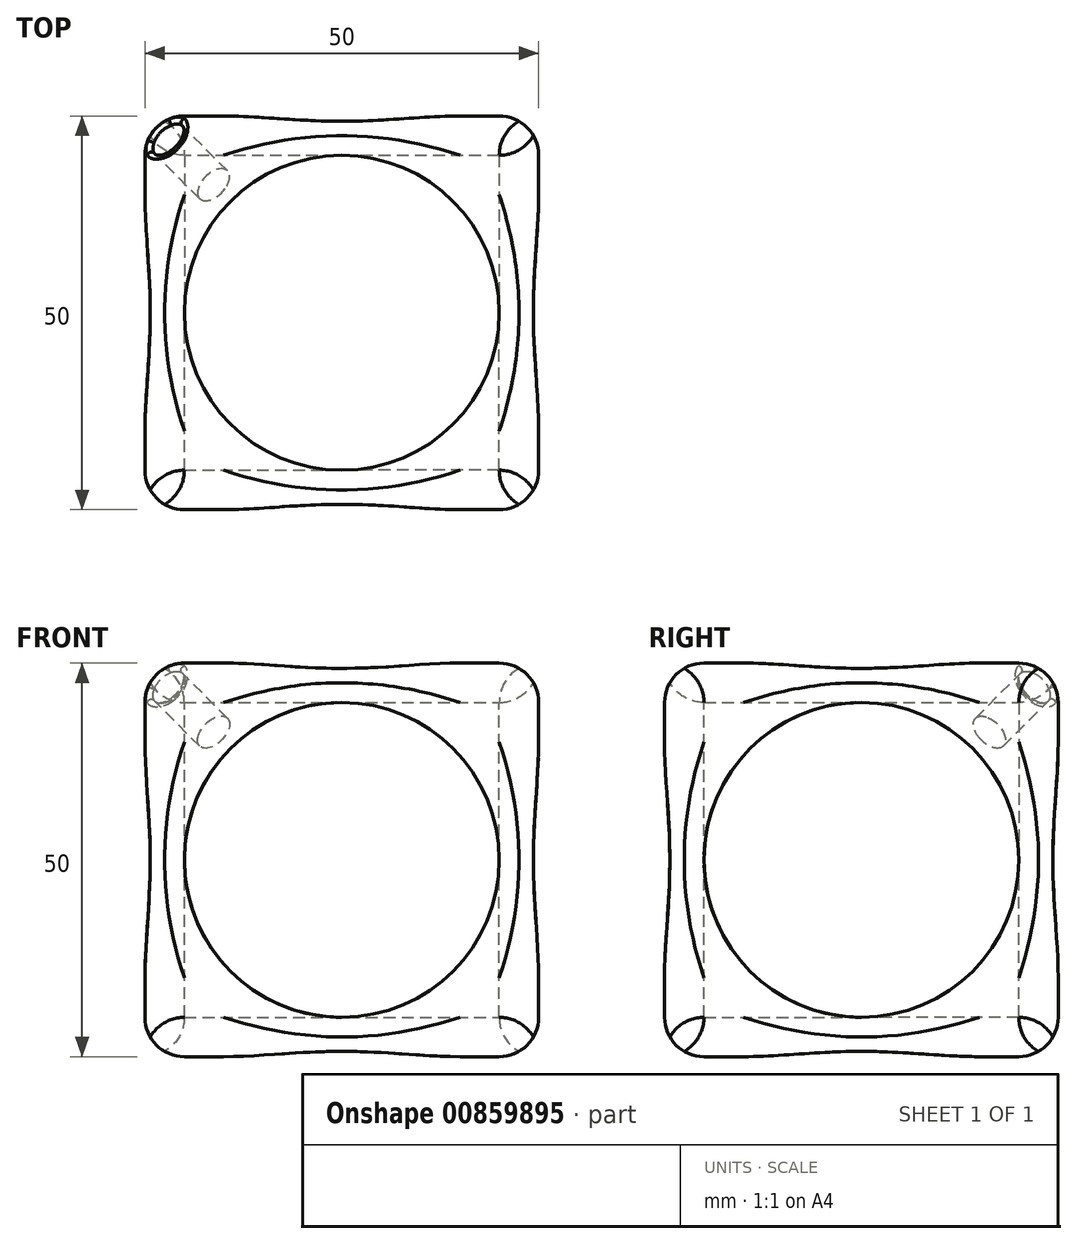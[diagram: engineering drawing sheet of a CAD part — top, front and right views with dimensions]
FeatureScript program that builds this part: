
annotation { "Feature Type Name" : "Feature", "Feature Type Description" : "" }
export const myFeature = defineFeature(function(context is Context, id is Id, definition is map)
    precondition{}
    {
        {
            var Q0;
            Q0=qCreatedBy(makeId("Top.planeOp"),FACE);
            var sketch = newSketch(context, id + "F0", { "sketchPlane" : qUnion([Q0])});
            skLineSegment(sketch, "E0.bottom", {"start": v(-25, -25) * mm, "end": v(25, -25) * mm});
            skLineSegment(sketch, "E0.top", {"start": v(-25, 25) * mm, "end": v(25, 25) * mm});
            skLineSegment(sketch, "E0.left", {"start": v(-25, -25) * mm, "end": v(-25, 25) * mm});
            skLineSegment(sketch, "E0.right", {"start": v(25, -25) * mm, "end": v(25, 25) * mm});
            skPoint(sketch, "E0.middle", {"position": v(0, 0) * mm});
            skSolve(sketch);
        }
        {
            var Q0;
            Q0 = qSketchRegion(id + "F0", true);
            extrude(context, id + "F1", {"entities" : qUnion([Q0]), "depth" : 50 * mm, "offsetDistance" : 25 * mm});
        }
        {
            var Q0;
            Q0=makeQuery(id+"F1.opExtrude","SWEPT_FACE",FACE,{"disambiguationData":[OSD([sQuery(id+"F0.wireOp",EDGE,"E0.left")])]});
            var sketch = newSketch(context, id + "F2", { "sketchPlane" : qUnion([Q0])});
            skCircle(sketch, "E1", {"center": v(0, 25) * mm, "radius": 20 * mm});
            skPoint(sketch, "E1.centerSnap0", {"position": v(25, 25) * mm});
            skSolve(sketch);
        }
        {
            var Q0;
            Q0=makeQuery(id+"F1.opExtrude","SWEPT_FACE",FACE,{"disambiguationData":[OSD([sQuery(id+"F0.wireOp",EDGE,"E0.top")])]});
            var sketch = newSketch(context, id + "F3", { "sketchPlane" : qUnion([Q0])});
            skCircle(sketch, "E2", {"center": v(0, 25) * mm, "radius": 20 * mm});
            skPoint(sketch, "E2.centerSnap0", {"position": v(25, 25) * mm});
            skSolve(sketch);
        }
        {
            var Q0;
            Q0=makeQuery(id+"F1.opExtrude","CAP_FACE",FACE,{"disambiguationData":[OSD([sQuery(id+"F0.wireOp",EDGE,"E0.bottom"),sQuery(id+"F0.wireOp",EDGE,"E0.top"),sQuery(id+"F0.wireOp",EDGE,"E0.left"),sQuery(id+"F0.wireOp",EDGE,"E0.right")])],"isStart":false});
            var sketch = newSketch(context, id + "F4", { "sketchPlane" : qUnion([Q0])});
            skCircle(sketch, "E3", {"center": v(0, 0) * mm, "radius": 20 * mm});
            skSolve(sketch);
        }
        {
            var Q0;
            Q0=makeQuery(id+"F4.imprint","IMPRINT",FACE,{"disambiguationData":[TD([[makeQuery(id+"F4.imprint","IMPRINT",EDGE,{"derivedFrom":sQuery(id+"F4.wireOp",EDGE,"E3")}),1.0]])]});
            extrude(context, id + "F5", {"entities" : qUnion([Q0]), "operationType" : NewBodyOperationType.REMOVE, "oppositeDirection" : true, "depth" : 50 * mm, "offsetDistance" : 25 * mm});
        }
        {
            var Q0;
            Q0=makeQuery(id+"F3.imprint","IMPRINT",FACE,{"disambiguationData":[TD([[makeQuery(id+"F3.imprint","IMPRINT",EDGE,{"derivedFrom":sQuery(id+"F3.wireOp",EDGE,"E2")}),1.0]])]});
            extrude(context, id + "F6", {"entities" : qUnion([Q0]), "operationType" : NewBodyOperationType.REMOVE, "oppositeDirection" : true, "depth" : 50 * mm, "offsetDistance" : 25 * mm});
        }
        {
            var Q0;
            Q0=makeQuery(id+"F2.imprint","IMPRINT",FACE,{"disambiguationData":[TD([[makeQuery(id+"F2.imprint","IMPRINT",EDGE,{"derivedFrom":sQuery(id+"F2.wireOp",EDGE,"E1")}),1.0]])]});
            extrude(context, id + "F7", {"entities" : qUnion([Q0]), "operationType" : NewBodyOperationType.REMOVE, "oppositeDirection" : true, "depth" : 50 * mm, "offsetDistance" : 25 * mm});
        }
        {
            var Q0;
            Q0=makeQuery(id+"F1.opExtrude","SWEPT_FACE",FACE,{"disambiguationData":[OSD([sQuery(id+"F0.wireOp",EDGE,"E0.left")])]});
            var Q1;
            Q1=makeQuery(id+"F1.opExtrude","SWEPT_FACE",FACE,{"disambiguationData":[OSD([sQuery(id+"F0.wireOp",EDGE,"E0.top")])]});
            var Q2;
            Q2=makeQuery(id+"F1.opExtrude","CAP_FACE",FACE,{"disambiguationData":[OSD([sQuery(id+"F0.wireOp",EDGE,"E0.bottom"),sQuery(id+"F0.wireOp",EDGE,"E0.top"),sQuery(id+"F0.wireOp",EDGE,"E0.left"),sQuery(id+"F0.wireOp",EDGE,"E0.right")])],"isStart":false});
            var Q3;
            Q3=makeQuery(id+"F1.opExtrude","SWEPT_FACE",FACE,{"disambiguationData":[OSD([sQuery(id+"F0.wireOp",EDGE,"E0.right")])]});
            var Q4;
            Q4=makeQuery(id+"F1.opExtrude","SWEPT_FACE",FACE,{"disambiguationData":[OSD([sQuery(id+"F0.wireOp",EDGE,"E0.bottom")])]});
            var Q5;
            Q5=makeQuery(id+"F1.opExtrude","CAP_FACE",FACE,{"disambiguationData":[OSD([sQuery(id+"F0.wireOp",EDGE,"E0.bottom"),sQuery(id+"F0.wireOp",EDGE,"E0.top"),sQuery(id+"F0.wireOp",EDGE,"E0.left"),sQuery(id+"F0.wireOp",EDGE,"E0.right")])],"isStart":true});
            fillet(context, id + "F8", {"entities" : qUnion([Q0, Q1, Q2, Q3, Q4, Q5]), "radius" : 5 * mm, "tangentPropagation" : true, "allowEdgeOverflow" : false});
        }
        {
            var Q0;
            Q0=qCreatedBy(makeId("Front.planeOp"),FACE);
            var sketch = newSketch(context, id + "F9", { "sketchPlane" : qUnion([Q0])});
            skLineSegment(sketch, "E4", {"start": v(0, 0) * mm, "end": v(0, 25) * mm});
            skCircle(sketch, "E5", {"center": v(0, 25) * mm, "radius": 28.27 * mm});
            skLineSegment(sketch, "E6", {"start": v(0, -3.27) * mm, "end": v(0, 53.28) * mm});
            skSolve(sketch);
        }
        {
            var Q0;
            {var subQ0=sQuery(id+"F9.wireOp",EDGE,"E4");Q0=makeQuery(id+"F9.imprint","IMPRINT",FACE,{"disambiguationData":[TD([[makeQuery(id+"F9.imprint","IMPRINT",EDGE,{"derivedFrom":subQ0}),-1.0]])]});}
            var Q1;
            Q1=sQuery(id+"F9.wireOp",EDGE,"E6");
            revolve(context, id + "F10", {"operationType" : NewBodyOperationType.REMOVE, "surfaceOperationType" : NewSurfaceOperationType.NEW, "entities" : qUnion([Q0]), "axis" : qUnion([Q1]), "revolveType" : RevolveType.FULL, "oppositeDirection" : true});
        }
        {
            var Q0;
            {var subQ0=sQuery(id+"F0.wireOp",EDGE,"E0.top");var subQ1=sQuery(id+"F0.wireOp",EDGE,"E0.left");Q0=makeQuery(id+"F8.opFillet","BLEND_VERTEX",VERTEX,{"blendedFrom":[makeQuery(id+"F1.opExtrude","CAP_VERTEX",VERTEX,{"disambiguationData":[OSD([subQ0,subQ1])],"isStart":false}),makeQuery(id+"F1.opExtrude","SWEPT_EDGE",EDGE,{"disambiguationData":[OSD([subQ0,subQ1])]}),makeQuery(id+"F1.opExtrude","CAP_EDGE",EDGE,{"disambiguationData":[OSD([subQ0])],"isStart":false}),makeQuery(id+"F1.opExtrude","SWEPT_FACE",FACE,{"disambiguationData":[OSD([subQ0])]})],"blendedInto":[makeQuery(id+"F1.opExtrude","SWEPT_FACE",FACE,{"disambiguationData":[OSD([subQ0])]})]});}
            var Q1;
            {var subQ0=sQuery(id+"F0.wireOp",EDGE,"E0.left");var subQ1=sQuery(id+"F0.wireOp",EDGE,"E0.top");Q1=makeQuery(id+"F8.opFillet","BLEND_VERTEX",VERTEX,{"blendedFrom":[makeQuery(id+"F1.opExtrude","CAP_VERTEX",VERTEX,{"disambiguationData":[OSD([subQ1,subQ0])],"isStart":false}),makeQuery(id+"F1.opExtrude","SWEPT_EDGE",EDGE,{"disambiguationData":[OSD([subQ1,subQ0])]}),makeQuery(id+"F1.opExtrude","CAP_EDGE",EDGE,{"disambiguationData":[OSD([subQ0])],"isStart":false}),makeQuery(id+"F1.opExtrude","SWEPT_FACE",FACE,{"disambiguationData":[OSD([subQ0])]})],"blendedInto":[makeQuery(id+"F1.opExtrude","SWEPT_FACE",FACE,{"disambiguationData":[OSD([subQ0])]})]});}
            var Q2;
            {var subQ0=sQuery(id+"F0.wireOp",EDGE,"E0.left");var subQ1=sQuery(id+"F0.wireOp",EDGE,"E0.top");Q2=makeQuery(id+"F8.opFillet","BLEND_VERTEX",VERTEX,{"blendedFrom":[makeQuery(id+"F1.opExtrude","CAP_VERTEX",VERTEX,{"disambiguationData":[OSD([subQ1,subQ0])],"isStart":false}),makeQuery(id+"F1.opExtrude","CAP_EDGE",EDGE,{"disambiguationData":[OSD([subQ1])],"isStart":false}),makeQuery(id+"F1.opExtrude","CAP_EDGE",EDGE,{"disambiguationData":[OSD([subQ0])],"isStart":false}),makeQuery(id+"F1.opExtrude","CAP_FACE",FACE,{"disambiguationData":[OSD([sQuery(id+"F0.wireOp",EDGE,"E0.bottom"),subQ1,subQ0,sQuery(id+"F0.wireOp",EDGE,"E0.right")])],"isStart":false})],"blendedInto":[makeQuery(id+"F1.opExtrude","CAP_FACE",FACE,{"disambiguationData":[OSD([sQuery(id+"F0.wireOp",EDGE,"E0.bottom"),subQ1,subQ0,sQuery(id+"F0.wireOp",EDGE,"E0.right")])],"isStart":false})]});}
            cPlane(context, id + "F11", {"entities" : qUnion([Q0, Q1, Q2]), "cplaneType" : CPlaneType.THREE_POINT, "offset" : 25 * mm, "width" : 150 * mm, "height" : 150 * mm});
        }
        {
            var Q0;
            Q0=qCreatedBy(id+"F11.planeOp",FACE);
            var sketch = newSketch(context, id + "F12", { "sketchPlane" : qUnion([Q0])});
            skCircle(sketch, "E7", {"center": v(10.17, 17.65) * mm, "radius": 2.5 * mm});
            skSolve(sketch);
        }
        {
            var Q0;
            Q0 = qSketchRegion(id + "F12", true);
            extrude(context, id + "F13", {"entities" : qUnion([Q0]), "operationType" : NewBodyOperationType.REMOVE, "endBound" : BoundingType.SYMMETRIC, "depth" : 100 * mm, "offsetDistance" : 25 * mm});
        }
        {
            var Q0;
            {var subQ0=sQuery(id+"F0.wireOp",EDGE,"E0.left");var subQ1=sQuery(id+"F0.wireOp",EDGE,"E0.top");Q0=makeQuery(id+"F13.boolean.opBoolean","INTERSECT",EDGE,{"derivedFrom":[makeQuery(id+"F8.opFillet","BLEND_FACE",FACE,{"disambiguationData":[OSD([subQ1,subQ0]),TDD([makeQuery(id+"F1.opExtrude","CAP_VERTEX",VERTEX,{"disambiguationData":[OSD([subQ1,subQ0])],"isStart":false})])]}),makeQuery(id+"F13.opExtrude","SWEPT_FACE",FACE,{"disambiguationData":[OSD([sQuery(id+"F12.wireOp",EDGE,"E7")])]})]});}
            fillet(context, id + "F14", {"entities" : qUnion([Q0]), "radius" : 0.5 * mm, "tangentPropagation" : true, "allowEdgeOverflow" : false});
        }
    });
